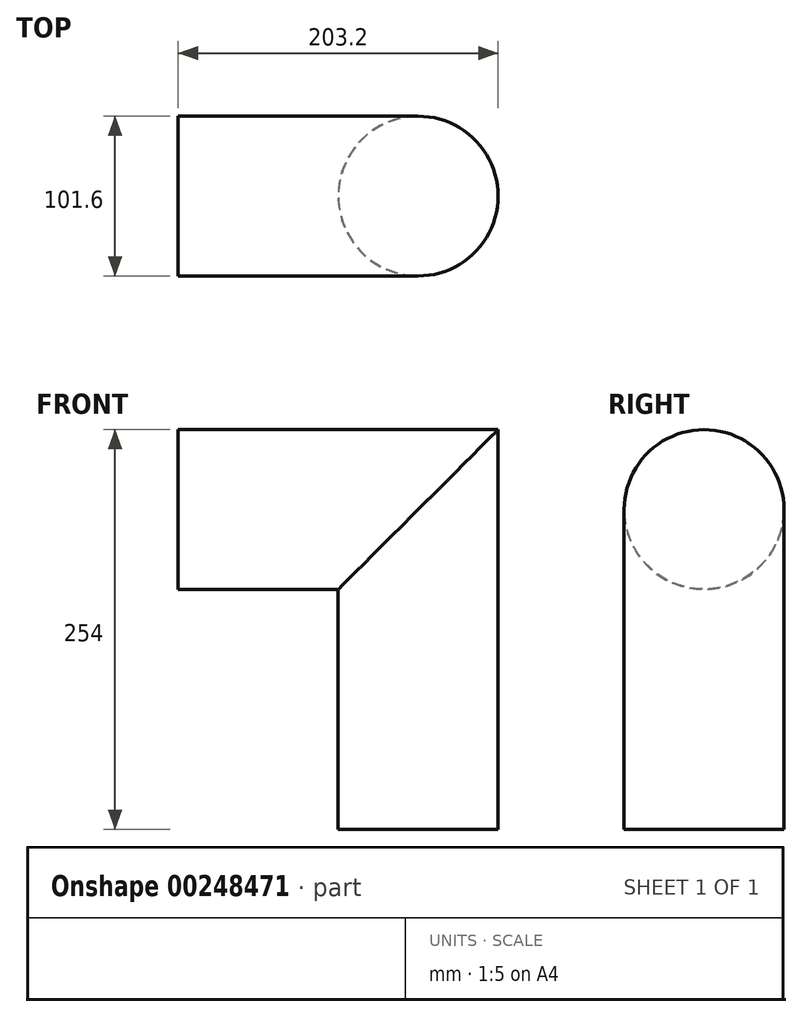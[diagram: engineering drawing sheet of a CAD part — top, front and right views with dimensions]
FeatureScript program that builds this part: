
annotation { "Feature Type Name" : "Feature", "Feature Type Description" : "" }
export const myFeature = defineFeature(function(context is Context, id is Id, definition is map)
    precondition{}
    {
        {
            var Q0;
            Q0=qCreatedBy(makeId("Top.planeOp"),FACE);
            var sketch = newSketch(context, id + "F0", { "sketchPlane" : qUnion([Q0])});
            skCircle(sketch, "E0", {"center": v(0, 0) * mm, "radius": 50.8 * mm});
            skSolve(sketch);
        }
        {
            var Q0;
            Q0=qCreatedBy(makeId("Front.planeOp"),FACE);
            var sketch = newSketch(context, id + "F1", { "sketchPlane" : qUnion([Q0])});
            skLineSegment(sketch, "E1", {"start": v(0, 0) * mm, "end": v(0, 203.2) * mm});
            skLineSegment(sketch, "E2", {"start": v(0, 203.2) * mm, "end": v(-152.4, 203.2) * mm});
            skSolve(sketch);
        }
        {
            var Q0;
            Q0=makeQuery(id+"F0.imprint","IMPRINT",FACE,{"disambiguationData":[TD([[makeQuery(id+"F0.imprint","IMPRINT",EDGE,{"derivedFrom":sQuery(id+"F0.wireOp",EDGE,"E0")}),1.0]])]});
            var Q1;
            Q1=sQuery(id+"F0.wireOp",EDGE,"E0");
            var Q2;
            Q2=sQuery(id+"F1.wireOp",EDGE,"E2");
            var Q3;
            Q3=sQuery(id+"F1.wireOp",EDGE,"E1");
            sweep(context, id + "F2", {"bodyType" : ToolBodyType.SURFACE, "profiles" : qUnion([Q0]), "surfaceProfiles" : qUnion([Q1]), "path" : qUnion([Q2, Q3])});
        }
    });
